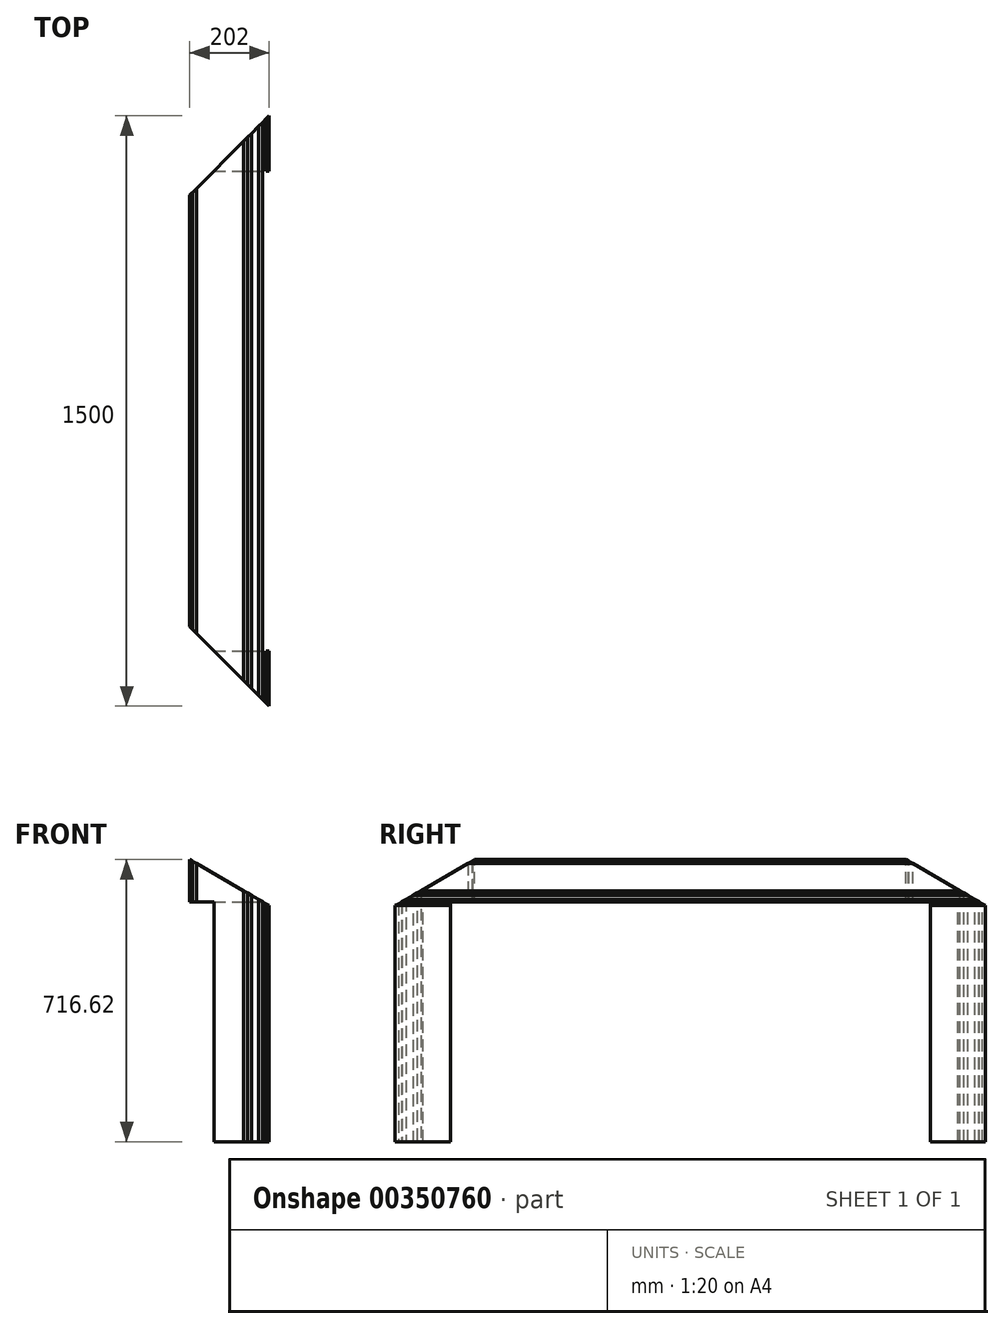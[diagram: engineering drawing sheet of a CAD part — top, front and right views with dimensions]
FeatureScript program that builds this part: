
annotation { "Feature Type Name" : "Feature", "Feature Type Description" : "" }
export const myFeature = defineFeature(function(context is Context, id is Id, definition is map)
    precondition{}
    {
        {
            var Q0;
            Q0=qCreatedBy(makeId("Right.planeOp"),FACE);
            var sketch = newSketch(context, id + "F0", { "sketchPlane" : qUnion([Q0])});
            skLineSegment(sketch, "E0", {"start": v(0, 0) * mm, "end": v(1500, 0) * mm});
            skLineSegment(sketch, "E1", {"start": v(1500, 0) * mm, "end": v(1500, 800) * mm});
            skLineSegment(sketch, "E2", {"start": v(1500, 800) * mm, "end": v(0, 800) * mm});
            skLineSegment(sketch, "E3", {"start": v(0, 800) * mm, "end": v(0, 0) * mm});
            skSolve(sketch);
        }
        {
            var Q0;
            Q0=makeQuery(id+"F0.imprint","IMPRINT",FACE,{"disambiguationData":[TD([[makeQuery(id+"F0.imprint","IMPRINT",EDGE,{"derivedFrom":sQuery(id+"F0.wireOp",EDGE,"E0")}),1.0]])]});
            extrude(context, id + "F1", {"entities" : qUnion([Q0]), "depth" : 6 * mm});
        }
        {
            var Q0;
            Q0=makeQuery(id+"F1.opExtrude","CAP_FACE",FACE,{"disambiguationData":[OSD([sQuery(id+"F0.wireOp",EDGE,"E0"),sQuery(id+"F0.wireOp",EDGE,"E1"),sQuery(id+"F0.wireOp",EDGE,"E2"),sQuery(id+"F0.wireOp",EDGE,"UxQu33BP-PdVc-IvKo-0Oal-Oq9sfbCTzBfW"),sQuery(id+"F0.wireOp",EDGE,"E3")])],"isStart":false});
            extrude(context, id + "F2", {"entities" : qUnion([Q0]), "depth" : 1 * mm});
        }
        {
            var Q0;
            Q0=makeQuery(id+"F2.opExtrude","CAP_FACE",FACE,{"disambiguationData":[OSD([sQuery(id+"F0.wireOp",EDGE,"E0"),sQuery(id+"F0.wireOp",EDGE,"E1"),sQuery(id+"F0.wireOp",EDGE,"E2"),sQuery(id+"F0.wireOp",EDGE,"UxQu33BP-PdVc-IvKo-0Oal-Oq9sfbCTzBfW"),sQuery(id+"F0.wireOp",EDGE,"E3")])],"isStart":false});
            extrude(context, id + "F3", {"entities" : qUnion([Q0]), "depth" : 10 * mm});
        }
        {
            var Q0;
            Q0=makeQuery(id+"F3.opExtrude","CAP_FACE",FACE,{"disambiguationData":[OSD([sQuery(id+"F0.wireOp",EDGE,"E0"),sQuery(id+"F0.wireOp",EDGE,"E1"),sQuery(id+"F0.wireOp",EDGE,"E2"),sQuery(id+"F0.wireOp",EDGE,"UxQu33BP-PdVc-IvKo-0Oal-Oq9sfbCTzBfW"),sQuery(id+"F0.wireOp",EDGE,"E3")])],"isStart":false});
            extrude(context, id + "F4", {"entities" : qUnion([Q0]), "depth" : 120 * mm});
        }
        {
            var Q0;
            Q0=makeQuery(id+"F4.opExtrude","CAP_FACE",FACE,{"disambiguationData":[OSD([sQuery(id+"F0.wireOp",EDGE,"E0"),sQuery(id+"F0.wireOp",EDGE,"E1"),sQuery(id+"F0.wireOp",EDGE,"E2"),sQuery(id+"F0.wireOp",EDGE,"UxQu33BP-PdVc-IvKo-0Oal-Oq9sfbCTzBfW"),sQuery(id+"F0.wireOp",EDGE,"E3")])],"isStart":false});
            extrude(context, id + "F5", {"entities" : qUnion([Q0]), "depth" : 10 * mm});
        }
        {
            var Q0;
            Q0=makeQuery(id+"F5.opExtrude","CAP_FACE",FACE,{"disambiguationData":[OSD([sQuery(id+"F0.wireOp",EDGE,"E0"),sQuery(id+"F0.wireOp",EDGE,"E1"),sQuery(id+"F0.wireOp",EDGE,"E2"),sQuery(id+"F0.wireOp",EDGE,"UxQu33BP-PdVc-IvKo-0Oal-Oq9sfbCTzBfW"),sQuery(id+"F0.wireOp",EDGE,"E3")])],"isStart":false});
            extrude(context, id + "F6", {"entities" : qUnion([Q0]), "depth" : 10 * mm});
        }
        {
            var Q0;
            Q0=makeQuery(id+"F6.opExtrude","CAP_FACE",FACE,{"disambiguationData":[OSD([sQuery(id+"F0.wireOp",EDGE,"E0"),sQuery(id+"F0.wireOp",EDGE,"E1"),sQuery(id+"F0.wireOp",EDGE,"E2"),sQuery(id+"F0.wireOp",EDGE,"UxQu33BP-PdVc-IvKo-0Oal-Oq9sfbCTzBfW"),sQuery(id+"F0.wireOp",EDGE,"E3")])],"isStart":false});
            extrude(context, id + "F7", {"entities" : qUnion([Q0]), "depth" : 18 * mm});
        }
        {
            var Q0;
            Q0=makeQuery(id+"F7.opExtrude","CAP_FACE",FACE,{"disambiguationData":[OSD([sQuery(id+"F0.wireOp",EDGE,"E0"),sQuery(id+"F0.wireOp",EDGE,"E1"),sQuery(id+"F0.wireOp",EDGE,"E2"),sQuery(id+"F0.wireOp",EDGE,"UxQu33BP-PdVc-IvKo-0Oal-Oq9sfbCTzBfW"),sQuery(id+"F0.wireOp",EDGE,"E3")])],"isStart":false});
            extrude(context, id + "F8", {"entities" : qUnion([Q0]), "depth" : 10 * mm});
        }
        {
            var Q0;
            Q0=makeQuery(id+"F8.opExtrude","CAP_FACE",FACE,{"disambiguationData":[OSD([sQuery(id+"F0.wireOp",EDGE,"E0"),sQuery(id+"F0.wireOp",EDGE,"E1"),sQuery(id+"F0.wireOp",EDGE,"E2"),sQuery(id+"F0.wireOp",EDGE,"E3")])],"isStart":false});
            extrude(context, id + "F9", {"entities" : qUnion([Q0]), "depth" : 1 * mm});
        }
        {
            var Q0;
            Q0=makeQuery(id+"F9.opExtrude","CAP_FACE",FACE,{"disambiguationData":[OSD([sQuery(id+"F0.wireOp",EDGE,"E0"),sQuery(id+"F0.wireOp",EDGE,"E1"),sQuery(id+"F0.wireOp",EDGE,"E2"),sQuery(id+"F0.wireOp",EDGE,"E3")])],"isStart":false});
            var sketch = newSketch(context, id + "F10", { "sketchPlane" : qUnion([Q0])});
            skLineSegment(sketch, "E4.bottom", {"start": v(0, 0) * mm, "end": v(70, 0) * mm});
            skLineSegment(sketch, "E4.top", {"start": v(0, 800) * mm, "end": v(70, 800) * mm});
            skLineSegment(sketch, "E4.left", {"start": v(0, 0) * mm, "end": v(0, 800) * mm});
            skLineSegment(sketch, "E4.right", {"start": v(70, 0) * mm, "end": v(70, 800) * mm});
            skLineSegment(sketch, "E5.bottom", {"start": v(1500, 0) * mm, "end": v(1430, 0) * mm});
            skLineSegment(sketch, "E5.top", {"start": v(1500, 800) * mm, "end": v(1430, 800) * mm});
            skLineSegment(sketch, "E5.left", {"start": v(1500, 0) * mm, "end": v(1500, 800) * mm});
            skLineSegment(sketch, "E5.right", {"start": v(1430, 0) * mm, "end": v(1430, 800) * mm});
            skSolve(sketch);
        }
        {
            var Q0;
            Q0=qSketchRegion(id+"F10",true);
            extrude(context, id + "F11", {"entities" : qUnion([Q0]), "depth" : 8 * mm});
        }
        {
            var Q0;
            Q0=makeQuery(id+"F11.opExtrude","CAP_FACE",FACE,{"disambiguationData":[OSD([sQuery(id+"F10.wireOp",EDGE,"E4.bottom"),sQuery(id+"F10.wireOp",EDGE,"E4.top"),sQuery(id+"F10.wireOp",EDGE,"E4.left"),sQuery(id+"F10.wireOp",EDGE,"E4.right")])],"isStart":false});
            var sketch = newSketch(context, id + "F12", { "sketchPlane" : qUnion([Q0])});
            skLineSegment(sketch, "E6.bottom", {"start": v(0, 0) * mm, "end": v(1500, 0) * mm});
            skLineSegment(sketch, "E6.top", {"start": v(0, 800) * mm, "end": v(1500, 800) * mm});
            skLineSegment(sketch, "E6.left", {"start": v(0, 0) * mm, "end": v(0, 800) * mm});
            skLineSegment(sketch, "E6.right", {"start": v(1500, 0) * mm, "end": v(1500, 800) * mm});
            skSolve(sketch);
        }
        {
            var Q0;
            Q0=qSketchRegion(id+"F12",true);
            extrude(context, id + "F13", {"entities" : qUnion([Q0]), "depth" : 8 * mm});
        }
        {
            var Q0;
            Q0=makeQuery(id+"F4.opExtrude","SWEPT_FACE",FACE,{"disambiguationData":[OSD([sQuery(id+"F0.wireOp",EDGE,"E2")])]});
            var sketch = newSketch(context, id + "F14", { "sketchPlane" : qUnion([Q0])});
            skLineSegment(sketch, "E7", {"start": v(202, 1500) * mm, "end": v(0, 1298) * mm});
            skLineSegment(sketch, "E8", {"start": v(0, 1298) * mm, "end": v(0, 1500) * mm});
            skLineSegment(sketch, "E9", {"start": v(0, 1500) * mm, "end": v(202, 1500) * mm});
            skLineSegment(sketch, "E10", {"start": v(0, 202) * mm, "end": v(202, 0) * mm});
            skLineSegment(sketch, "E11", {"start": v(202, 0) * mm, "end": v(0, 0) * mm});
            skLineSegment(sketch, "E12", {"start": v(0, 0) * mm, "end": v(0, 202) * mm});
            skSolve(sketch);
        }
        {
            var Q0;
            Q0=qSketchRegion(id+"F14",true);
            extrude(context, id + "F15", {"entities" : qUnion([Q0]), "operationType" : NewBodyOperationType.REMOVE, "endBound" : BoundingType.THROUGH_ALL, "oppositeDirection" : true, "depth" : 25 * mm});
        }
        {
            var Q0;
            Q0=makeQuery(id+"F13.opExtrude","CAP_FACE",FACE,{"disambiguationData":[OSD([sQuery(id+"F12.wireOp",EDGE,"E6.bottom"),sQuery(id+"F12.wireOp",EDGE,"E6.top"),sQuery(id+"F12.wireOp",EDGE,"E6.left"),sQuery(id+"F12.wireOp",EDGE,"E6.right")])],"isStart":false});
            var sketch = newSketch(context, id + "F16", { "sketchPlane" : qUnion([Q0])});
            skLineSegment(sketch, "E13.bottom", {"start": v(140.4, 0) * mm, "end": v(1359.6, 0) * mm});
            skLineSegment(sketch, "E13.top", {"start": v(140.4, 609.6) * mm, "end": v(1359.6, 609.6) * mm});
            skLineSegment(sketch, "E13.left", {"start": v(140.4, 0) * mm, "end": v(140.4, 609.6) * mm});
            skLineSegment(sketch, "E13.right", {"start": v(1359.6, 0) * mm, "end": v(1359.6, 609.6) * mm});
            skLineSegment(sketch, "E14", {"start": v(140.4, 0) * mm, "end": v(0, 0) * mm, "construction": true});
            skLineSegment(sketch, "E15", {"start": v(1359.6, 0) * mm, "end": v(1500, 0) * mm, "construction": true});
            skSolve(sketch);
        }
        {
            var Q0;
            Q0 = qSketchRegion(id + "F16", true);
            extrude(context, id + "F17", {"entities" : qUnion([Q0]), "operationType" : NewBodyOperationType.REMOVE, "endBound" : BoundingType.THROUGH_ALL, "oppositeDirection" : true, "depth" : 25 * mm});
        }
        {
            var Q0;
            Q0=qCreatedBy(makeId("Front.planeOp"),FACE);
            var sketch = newSketch(context, id + "F18", { "sketchPlane" : qUnion([Q0])});
            skLineSegment(sketch, "E16", {"start": v(202, 0) * mm, "end": v(202, 600) * mm, "construction": true});
            skLineSegment(sketch, "E17", {"start": v(-664.03, 1100) * mm, "end": v(-1298, 1100) * mm, "construction": true});
            skLineSegment(sketch, "E18", {"start": v(-1298, 1100) * mm, "end": v(-1298, 0) * mm, "construction": true});
            skLineSegment(sketch, "E19", {"start": v(-1298, 0) * mm, "end": v(202, 0) * mm, "construction": true});
            skLineSegment(sketch, "E20", {"start": v(-664.03, 1100) * mm, "end": v(202, 600) * mm});
            skLineSegment(sketch, "E21", {"start": v(202, 1100) * mm, "end": v(-664.03, 1100) * mm});
            skLineSegment(sketch, "E22", {"start": v(202, 1100) * mm, "end": v(202, 600) * mm});
            skSolve(sketch);
        }
        {
            var Q0;
            Q0=makeQuery(id+"F18.imprint","IMPRINT",FACE,{"disambiguationData":[TD([[makeQuery(id+"F18.imprint","IMPRINT",EDGE,{"derivedFrom":sQuery(id+"F18.wireOp",EDGE,"E20")}),1.0]])]});
            extrude(context, id + "F19", {"entities" : qUnion([Q0]), "operationType" : NewBodyOperationType.REMOVE, "endBound" : BoundingType.THROUGH_ALL, "oppositeDirection" : true, "depth" : 25 * mm});
        }
    });
